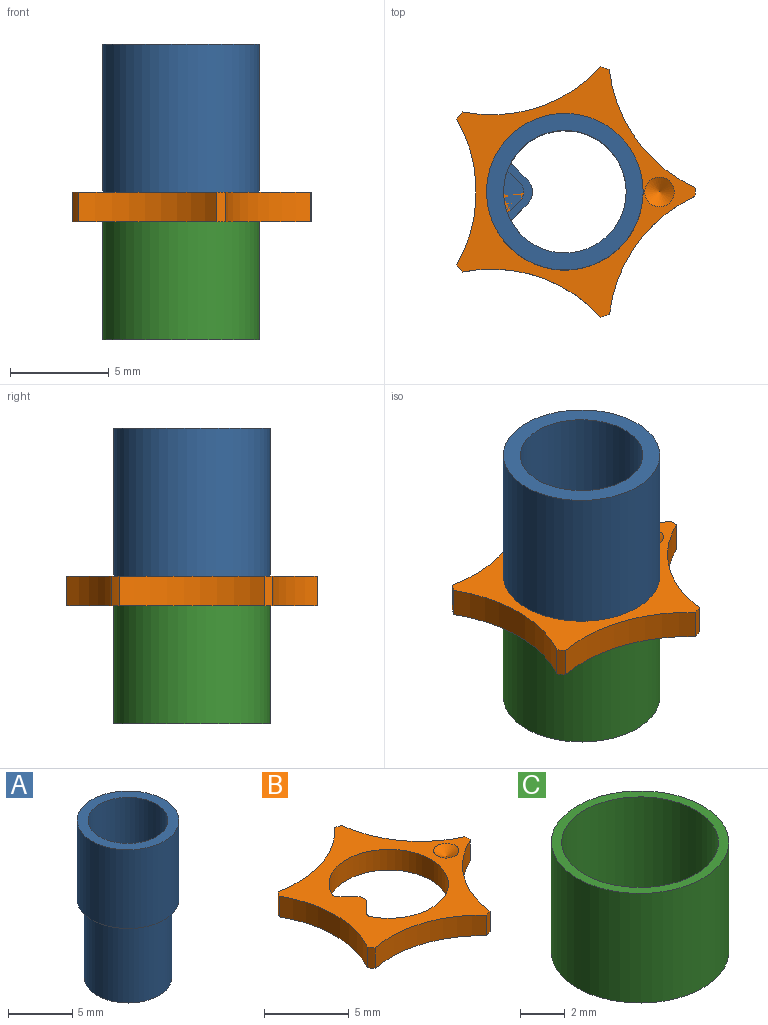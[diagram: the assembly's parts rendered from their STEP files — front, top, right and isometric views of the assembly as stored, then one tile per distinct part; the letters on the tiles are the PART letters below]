
ASSEMBLY  parts=3 mates=1
PART A: 12 faces, bbox 7.9x7.9x15 mm
  f0: cylinder r=3.11mm len=15mm, axis (0,0,-1), area 268.3mm2, adj f2,f4,f6,f7,f11
  f1: cylinder r=3.97mm len=7.94mm, axis (0,0,-1), area 187.1mm2, adj f2,f3
  f2: plane 7.94x7.94mm, normal (0,0,1), area 19.2mm2, adj f0,f1
  f3: plane 7.94x7.94mm, normal (0,0,-1), area 13.3mm2, adj f1,f10
  f4: plane 3.13x1.46mm, normal (0,0,1), area 2.7mm2, adj f0,f5,f6,f7,f8,f9
  f5: plane 7.5x0.75mm, normal (0.71,-0.71,0), area 7.9mm2, adj f4,f6,f9,f11
  f6: cylinder r=0.15mm len=7.5mm, axis (0,0,1), area 1.5mm2, adj f0,f4,f5,f11
  f7: cylinder r=0.15mm len=7.5mm, axis (0,0,1), area 1.5mm2, adj f0,f4,f8,f11
  f8: plane 7.5x0.75mm, normal (0.71,0.71,0), area 7.9mm2, adj f4,f7,f9,f11
  f9: cylinder r=0.9mm len=7.5mm, axis (0,0,1), area 10.6mm2, adj f4,f5,f8,f11
  f10: cylinder r=3.4mm len=7.5mm, axis (0,0,1), area 160mm2, adj f3,f11
  f11: plane 6.79x6.79mm, normal (0,0,-1), area 8.6mm2, adj f0,f5,f6,f7,f8,f9,f10
PART B: 19 faces, bbox 12.1x12.7x1.5 mm
  f0: cylinder r=7.5mm len=7.03mm, axis (0,0,-1), area 11.6mm2, adj f1,f15,f16,f17
  f1: cylinder r=6.6mm len=1.5mm, axis (0,0,-1), area 0.7mm2, adj f0,f2,f16,f17
  f2: cylinder r=7.5mm len=7.39mm, axis (0,0,-1), area 11.6mm2, adj f1,f3,f16,f17
  f3: cylinder r=6.6mm len=1.5mm, axis (0,0,-1), area 0.7mm2, adj f2,f4,f16,f17
  f4: cylinder r=7.5mm len=7.02mm, axis (0,0,-1), area 11.6mm2, adj f3,f5,f16,f17
  f5: cylinder r=6.6mm len=1.5mm, axis (0,0,-1), area 0.7mm2, adj f4,f6,f16,f17
  f6: cylinder r=7.5mm len=5.97mm, axis (0,0,-1), area 11.6mm2, adj f5,f7,f16,f17
  f7: cylinder r=6.6mm len=1.5mm, axis (0,0,-1), area 0.7mm2, adj f6,f8,f16,f17
  f8: cylinder r=7.5mm len=5.98mm, axis (0,0,-1), area 11.6mm2, adj f7,f15,f16,f17
  f9: cylinder r=3.53mm len=7.06mm, axis (0,0,-1), area 28.3mm2, adj f10,f14,f16,f17
  f10: cylinder r=0.3mm len=1.5mm, axis (0,0,-1), area 0.6mm2, adj f9,f11,f16,f17
  f11: plane 1.5x0.83mm, normal (0.71,-0.71,0), area 1.8mm2, adj f10,f12,f16,f17
  f12: cylinder r=0.6mm len=1.5mm, axis (0,0,-1), area 1.4mm2, adj f11,f13,f16,f17
  f13: plane 1.5x0.83mm, normal (0.71,0.71,0), area 1.8mm2, adj f12,f14,f16,f17
  f14: cylinder r=0.3mm len=1.5mm, axis (0,0,-1), area 0.6mm2, adj f9,f13,f16,f17
  f15: cylinder r=6.6mm len=1.5mm, axis (0,0,-1), area 0.7mm2, adj f0,f8,f16,f17
  f16: plane 12.69x12.07mm, normal (0,0,1), area 45.8mm2, adj f0,f1,f2,f3,f4,f5,f6,f7
  f17: plane 12.69x12.07mm, normal (0,0,-1), area 47.6mm2, adj f0,f1,f2,f3,f4,f5,f6,f7
  f18: cone r=0.75mm half-angle=60deg, axis (0,0,1), area 2mm2, adj f16
PART C: 4 faces, bbox 7.9x7.9x6 mm
  f0: cylinder r=3.51mm len=7.02mm, axis (0,0,-1), area 132.3mm2, adj f2,f3
  f1: cylinder r=3.97mm len=7.94mm, axis (0,0,-1), area 149.7mm2, adj f2,f3
  f2: plane 7.94x7.94mm, normal (0,0,1), area 10.8mm2, adj f0,f1
  f3: plane 7.94x7.94mm, normal (0,0,-1), area 10.8mm2, adj f0,f1
PLACE A at identity fixed
PLACE B t=(0,0,-1.5)mm
PLACE C t=(0,0,-7.5)mm
MATE fastened B.f1 <-> C.f0  axis (0,0,-1) through (0,0,-1.5)mm
